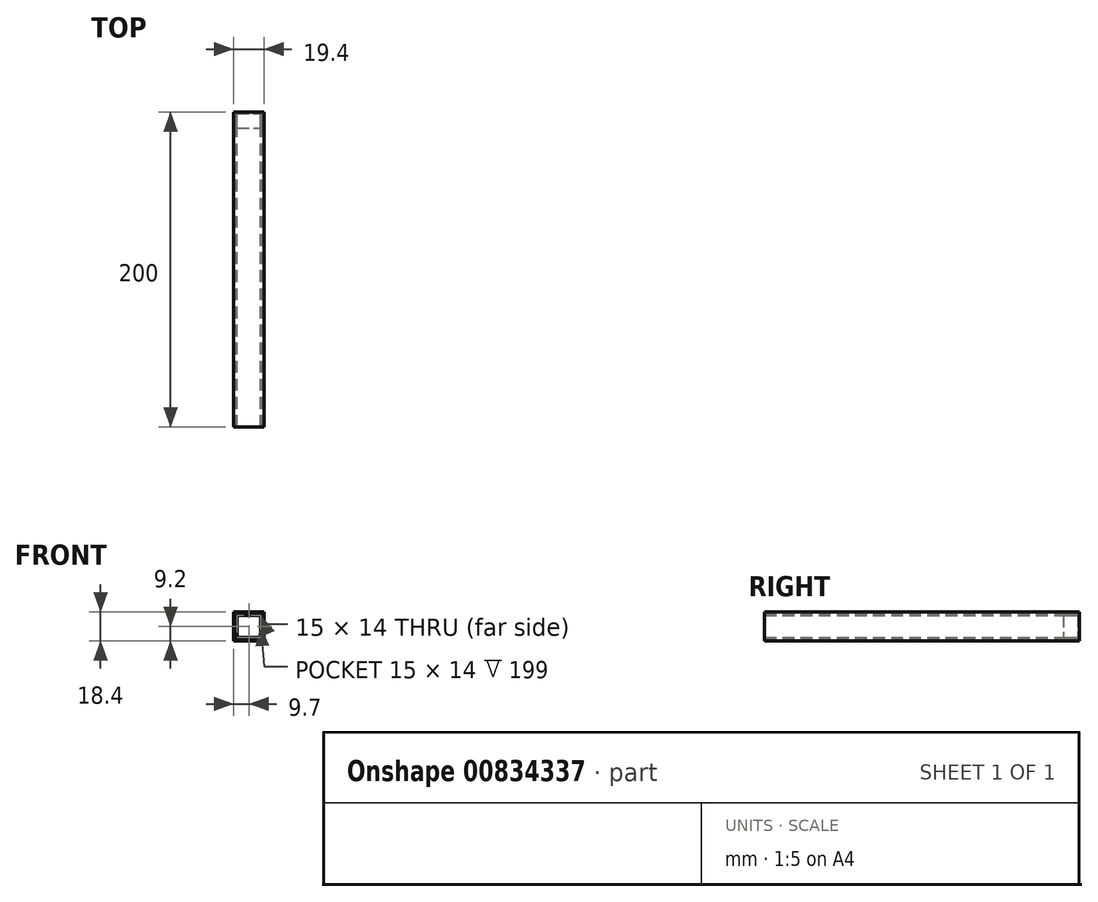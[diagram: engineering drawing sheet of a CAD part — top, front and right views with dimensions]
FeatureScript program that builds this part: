
annotation { "Feature Type Name" : "Feature", "Feature Type Description" : "" }
export const myFeature = defineFeature(function(context is Context, id is Id, definition is map)
    precondition{}
    {
        {
            var Q0;
            Q0=qCreatedBy(makeId("Front.planeOp"),FACE);
            var sketch = newSketch(context, id + "F0", { "sketchPlane" : qUnion([Q0])});
            skLineSegment(sketch, "E0.bottom", {"start": v(-7.5, 7) * mm, "end": v(7.5, 7) * mm});
            skLineSegment(sketch, "E0.top", {"start": v(-7.5, -7) * mm, "end": v(7.5, -7) * mm});
            skLineSegment(sketch, "E0.left", {"start": v(-7.5, 7) * mm, "end": v(-7.5, -7) * mm});
            skLineSegment(sketch, "E0.right", {"start": v(7.5, 7) * mm, "end": v(7.5, -7) * mm});
            skPoint(sketch, "E0.middle", {"position": v(0, 0) * mm});
            skLineSegment(sketch, "E1.0", {"start": v(-8.5, 8) * mm, "end": v(8.5, 8) * mm});
            skLineSegment(sketch, "E1.1", {"start": v(-8.5, 8) * mm, "end": v(-8.5, -8) * mm});
            skLineSegment(sketch, "E1.2", {"start": v(-8.5, -8) * mm, "end": v(8.5, -8) * mm});
            skLineSegment(sketch, "E1.3", {"start": v(8.5, 8) * mm, "end": v(8.5, -8) * mm});
            skLineSegment(sketch, "E2.0", {"start": v(-8.7, 8.2) * mm, "end": v(8.7, 8.2) * mm});
            skLineSegment(sketch, "E2.1", {"start": v(-8.7, 8.2) * mm, "end": v(-8.7, -8.2) * mm});
            skLineSegment(sketch, "E2.2", {"start": v(-8.7, -8.2) * mm, "end": v(8.7, -8.2) * mm});
            skLineSegment(sketch, "E2.3", {"start": v(8.7, 8.2) * mm, "end": v(8.7, -8.2) * mm});
            skLineSegment(sketch, "E3.0", {"start": v(-9.7, 9.2) * mm, "end": v(9.7, 9.2) * mm});
            skLineSegment(sketch, "E3.1", {"start": v(-9.7, 9.2) * mm, "end": v(-9.7, -9.2) * mm});
            skLineSegment(sketch, "E3.2", {"start": v(-9.7, -9.2) * mm, "end": v(9.7, -9.2) * mm});
            skLineSegment(sketch, "E3.3", {"start": v(9.7, 9.2) * mm, "end": v(9.7, -9.2) * mm});
            skSolve(sketch);
        }
        {
            var Q0;
            Q0=makeQuery(id+"F0.imprint","IMPRINT",FACE,{"disambiguationData":[TD([[makeQuery(id+"F0.imprint","IMPRINT",EDGE,{"derivedFrom":sQuery(id+"F0.wireOp",EDGE,"E0.bottom")}),1.0]])]});
            extrude(context, id + "F1", {"entities" : qUnion([Q0]), "depth" : 200 * mm, "offsetDistance" : 25 * mm});
        }
        {
            var Q0;
            Q0=makeQuery(id+"F0.imprint","IMPRINT",FACE,{"disambiguationData":[TD([[makeQuery(id+"F0.imprint","IMPRINT",EDGE,{"derivedFrom":sQuery(id+"F0.wireOp",EDGE,"E0.bottom")}),-1.0]])]});
            extrude(context, id + "F2", {"entities" : qUnion([Q0]), "operationType" : NewBodyOperationType.ADD, "depth" : 1 * mm, "offsetDistance" : 25 * mm});
        }
        {
            var Q0;
            Q0=makeQuery(id+"F0.imprint","IMPRINT",FACE,{"disambiguationData":[TD([[makeQuery(id+"F0.imprint","IMPRINT",EDGE,{"derivedFrom":sQuery(id+"F0.wireOp",EDGE,"E2.0")}),1.0]])]});
            extrude(context, id + "F3", {"entities" : qUnion([Q0]), "depth" : 200 * mm, "offsetDistance" : 25 * mm});
        }
        {
            var Q0;
            Q0=makeQuery(id+"F0.imprint","IMPRINT",FACE,{"disambiguationData":[TD([[makeQuery(id+"F0.imprint","IMPRINT",EDGE,{"derivedFrom":sQuery(id+"F0.wireOp",EDGE,"E1.0")}),1.0]])]});
            var Q1;
            Q1=makeQuery(id+"F0.imprint","IMPRINT",FACE,{"disambiguationData":[TD([[makeQuery(id+"F0.imprint","IMPRINT",EDGE,{"derivedFrom":sQuery(id+"F0.wireOp",EDGE,"E0.bottom")}),1.0]])]});
            var Q2;
            Q2=makeQuery(id+"F0.imprint","IMPRINT",FACE,{"disambiguationData":[TD([[makeQuery(id+"F0.imprint","IMPRINT",EDGE,{"derivedFrom":sQuery(id+"F0.wireOp",EDGE,"E0.bottom")}),-1.0]])]});
            extrude(context, id + "F4", {"entities" : qUnion([Q0, Q1, Q2]), "operationType" : NewBodyOperationType.ADD, "depth" : 1 * mm, "offsetDistance" : 25 * mm});
        }
        {
            var Q0;
            Q0=makeQuery(id+"F0.imprint","IMPRINT",FACE,{"disambiguationData":[TD([[makeQuery(id+"F0.imprint","IMPRINT",EDGE,{"derivedFrom":sQuery(id+"F0.wireOp",EDGE,"E0.bottom")}),1.0]])]});
            extrude(context, id + "F5", {"entities" : qUnion([Q0]), "depth" : 10 * mm, "offsetDistance" : 25 * mm});
        }
    });
